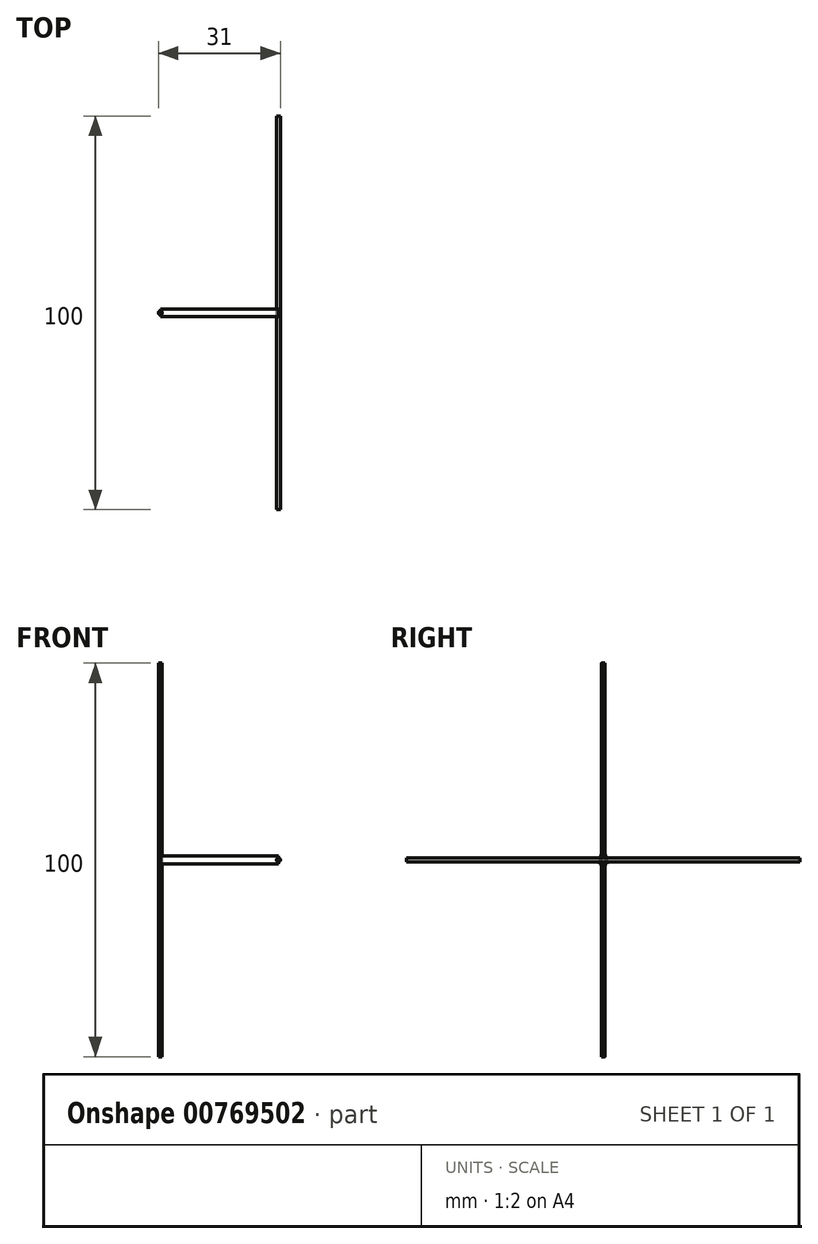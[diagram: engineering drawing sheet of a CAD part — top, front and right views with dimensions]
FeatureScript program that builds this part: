
annotation { "Feature Type Name" : "Feature", "Feature Type Description" : "" }
export const myFeature = defineFeature(function(context is Context, id is Id, definition is map)
    precondition{}
    {
        {
            var Q0;
            Q0=qCreatedBy(makeId("Top.planeOp"),FACE);
            var sketch = newSketch(context, id + "F0", { "sketchPlane" : qUnion([Q0])});
            skLineSegment(sketch, "E0", {"start": v(0, 50) * mm, "end": v(0, -50) * mm});
            skPoint(sketch, "E1", {"position": v(0, 0) * mm});
            skSolve(sketch);
        }
        {
            var Q0;
            Q0=qCreatedBy(makeId("Right.planeOp"),FACE);
            cPlane(context, id + "F1", {"entities" : qUnion([Q0]), "cplaneType" : CPlaneType.OFFSET, "offset" : 30 * mm, "oppositeDirection" : true, "width" : 150 * mm, "height" : 150 * mm});
        }
        {
            var Q0;
            Q0=qCreatedBy(id+"F1.planeOp",FACE);
            var sketch = newSketch(context, id + "F2", { "sketchPlane" : qUnion([Q0])});
            skLineSegment(sketch, "E2", {"start": v(0, 50) * mm, "end": v(0, -50) * mm});
            skSolve(sketch);
        }
        {
            var Q0;
            Q0=qCreatedBy(makeId("Front.planeOp"),FACE);
            var sketch = newSketch(context, id + "F3", { "sketchPlane" : qUnion([Q0])});
            skCircle(sketch, "E3", {"center": v(0, 0) * mm, "radius": 0.5 * mm});
            skSolve(sketch);
        }
        {
            var Q0;
            Q0 = qSketchRegion(id + "F3", true);
            extrude(context, id + "F4", {"entities" : qUnion([Q0]), "depth" : 100 * mm, "offsetDistance" : 25 * mm, "symmetric" : true});
        }
        {
            var Q0;
            Q0=qCreatedBy(makeId("Top.planeOp"),FACE);
            var sketch = newSketch(context, id + "F5", { "sketchPlane" : qUnion([Q0])});
            skCircle(sketch, "E4", {"center": v(-30, 0) * mm, "radius": 0.5 * mm});
            skSolve(sketch);
        }
        {
            var Q0;
            Q0 = qSketchRegion(id + "F5", true);
            extrude(context, id + "F6", {"entities" : qUnion([Q0]), "depth" : 100 * mm, "offsetDistance" : 25 * mm, "symmetric" : true});
        }
        {
            var Q0;
            Q0=qCreatedBy(makeId("Right.planeOp"),FACE);
            var sketch = newSketch(context, id + "F7", { "sketchPlane" : qUnion([Q0])});
            skLineSegment(sketch, "E5.bottom", {"start": v(1, 1) * mm, "end": v(-1, 1) * mm});
            skLineSegment(sketch, "E5.top", {"start": v(1, -1) * mm, "end": v(-1, -1) * mm});
            skLineSegment(sketch, "E5.left", {"start": v(1, 1) * mm, "end": v(1, -1) * mm});
            skLineSegment(sketch, "E5.right", {"start": v(-1, 1) * mm, "end": v(-1, -1) * mm});
            skPoint(sketch, "E5.middle", {"position": v(0, 0) * mm});
            skSolve(sketch);
        }
        {
            var Q0;
            Q0 = qSketchRegion(id + "F7", true);
            extrude(context, id + "F8", {"entities" : qUnion([Q0]), "oppositeDirection" : true, "depth" : 30 * mm, "offsetDistance" : 25 * mm});
        }
    });
